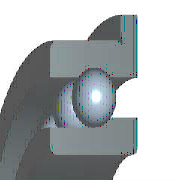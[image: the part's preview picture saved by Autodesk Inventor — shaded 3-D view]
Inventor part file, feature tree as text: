
AUTODESK INVENTOR PART (.ipt)
format: ipt  version: 2020 (Build 240168000, 168)  size: 329,728 bytes
history: native  units: mm (DEFAULTED — no unit token found)
features: other x1, pattern_circular x1
ambient origin geometry x8: Origin, YZ Plane, XZ Plane, XY Plane, X Axis, Y Axis, Z Axis, Center Point
bodies: Solid1 (feature_tree), Body (feature_tree)
feature tree (2):
  other  "Ball"
  pattern_circular  "Balls"  [2 undecoded]
note: 2 required parameter values undecoded (feature->parameter linkage not recoverable at this tier; creation-order binding heuristic only, values carry confidence <= 0.55)
